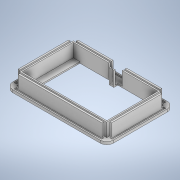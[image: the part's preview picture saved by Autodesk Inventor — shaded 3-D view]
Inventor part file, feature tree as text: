
AUTODESK INVENTOR PART (.ipt)
format: ipt  version: 2021 (Build 250183000, 183)  size: 337,920 bytes
history: native  units: mm
features: extrude x8, sketch x6, projected_geometry x5
ambient origin geometry x8: Origin, YZ Plane, XZ Plane, XY Plane, X Axis, Y Axis, Z Axis, Center Point
bodies: Volumenkörper1 (feature_tree)
feature tree (19):
  extrude  "Extrusion1"  Depth=100.0mm
  sketch  "Skizze2"  dims[d2=10.0mm d3=2.0mm d4=0.0mm]
  extrude  "Extrusion2"  Depth=2.0mm TaperAngle=0.0deg
  extrude  "Extrusion4"  Depth=2.0mm
  extrude  "Extrusion5"  Depth=2.0mm
  extrude  "Extrusion6"  Depth=0.5mm
  extrude  "Extrusion8"  Depth=2.0mm TaperAngle=0.0deg
  sketch  "Skizze7"  dims[d15=2.0mm d16=2.0mm d17=0.0mm d20=20.0mm d21=0.0mm d22=0.5mm d23=10.0mm d24=0.0mm d25=10.0mm d26=0.0mm d27=0.0mm d31=20.0mm d32=10.0mm d33=0.0mm d37=10.0mm d38=0.0mm d39=6.0mm d40=7.0mm d41=2.0mm d42=2.0mm d43=0.0mm]
  extrude  "Extrusion9"  Depth=20.0mm TaperAngle=0.0deg
  extrude  "Extrusion10"  Depth=0.5mm
  sketch  "Skizze1"  dims[d0=150.0mm d1=100.0mm]
  projected_geometry  "Projizierte Kontur1"
  sketch  "Skizze3"  dims[d5=3.5mm d6=2.0mm]
  projected_geometry  "Projizierte Kontur2"
  sketch  "Skizze4"  dims[d7=2.0mm d12=2.0mm]
  projected_geometry  "Projizierte Kontur3"
  sketch  "Skizze6"  dims[d13=2.0mm d14=0.5mm]
  projected_geometry  "Projizierte Kontur5"
  projected_geometry  "Projizierte Kontur6"
